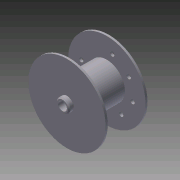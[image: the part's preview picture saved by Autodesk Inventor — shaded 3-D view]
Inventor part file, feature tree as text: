
AUTODESK INVENTOR PART (.ipt)
format: ipt  version: 2011 (Build 150239000, 239)  size: 233,984 bytes
history: native  units: in
note: dims shown in document units (in); Inventor stores cm internally (conversion verified against a paired STEP export)
features: extrude x10, sketch x10, projected_geometry x5, chamfer x2, plane x1, pattern_circular x1, reference x1
ambient origin geometry x8: Origin, YZ Plane, XZ Plane, XY Plane, X Axis, Y Axis, Z Axis, Center Point
bodies: Solid1 (feature_tree)
feature tree (30):
  extrude  "Extrusion1"  Depth=0.115in TaperAngle=0.0deg
  extrude  "Extrusion2"  Depth=2.105in TaperAngle=0.0deg
  extrude  "Extrusion3"  Depth=0.75in
  extrude  "Extrusion4"  Depth=0.49in
  sketch  "Sketch5"  dims[d12=0.75in d13=0.5in d14=0.0in]
  extrude  "Extrusion5"  Depth=0.5in TaperAngle=0.0deg
  extrude  "Extrusion6"  Depth=0.115in
  extrude  "Extrusion7"  Depth=0.0625in TaperAngle=45.0deg
  chamfer  "Chamfer1"  Distance=0.5in
  plane  "Work Plane1"
  extrude  "Extrusion8"  Depth=2.245in
  pattern_circular  "Circular Pattern1"  [2 undecoded]
  extrude  "Extrusion9"  Depth=0.025in TaperAngle=0.0deg
  chamfer  "Chamfer2"  Distance=0.025in Angle=45.0deg
  extrude  "Extrusion11"  Depth=1.0in TaperAngle=0.0deg
  sketch  "Sketch1"  dims[d0=4.315in d1=0.115in d2=0.0in]
  sketch  "Sketch2"  dims[d3=2.022in d4=2.105in d5=0.0in]
  sketch  "Sketch3"  dims[d6=0.115in d7=0.0in d8=0.75in]
  projected_geometry  "Projected Loop1"
  sketch  "Sketch4"  dims[d9=0.25in d10=0.0in d11=0.49in]
  sketch  "Sketch6"  dims[d15=0.5in d16=0.0in d17=0.115in]
  projected_geometry  "Projected Loop2"
  sketch  "Sketch7"  dims[d18=0.5in d19=0.0in d20=0.0625in d21=0.125in d22=45.0deg]
  projected_geometry  "Projected Loop3"
  sketch  "Sketch8"  dims[d23=0.575in]
  projected_geometry  "Projected Loop4"
  projected_geometry  "Projected Loop5"
  sketch  "Sketch9"  dims[d24=0.653in d25=0.5in d26=0.0in]
  sketch  "Sketch12"  dims[d27=0.7874in d28=90.0deg d30=2.245in d31=3.855in d32=0.025in d33=0.0in d34=0.025in d35=0.125in d36=45.0deg d52=1.0in d53=0.0in]
  reference  "Reference1"
note: 2 required parameter values undecoded (feature->parameter linkage not recoverable at this tier; creation-order binding heuristic only, values carry confidence <= 0.55)
